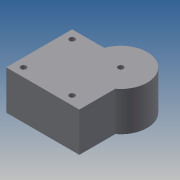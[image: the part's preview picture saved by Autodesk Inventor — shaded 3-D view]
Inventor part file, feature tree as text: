
AUTODESK INVENTOR PART (.ipt)
format: ipt  version: 2013 (Build 170138000, 138)  size: 100,864 bytes
history: native  units: mm
features: extrude x3, sketch x3
ambient origin geometry x8: Origin, YZ Plane, XZ Plane, XY Plane, X Axis, Y Axis, Z Axis, Center Point
bodies: Solid1 (feature_tree)
feature tree (6):
  extrude  "Extrusion1"  Depth=5.5mm
  extrude  "Extrusion2"  Depth=25.0mm TaperAngle=0.0deg
  extrude  "Extrusion3"  Depth=16.9mm
  sketch  "Sketch1"  dims[d0=42.0mm d1=5.5mm]
  sketch  "Sketch2"  dims[d2=3.5mm d3=25.0mm d4=0.0mm]
  sketch  "Sketch3"  dims[d5=4.6mm d6=0.0mm d7=16.9mm d9=4.6mm d10=0.0mm]
